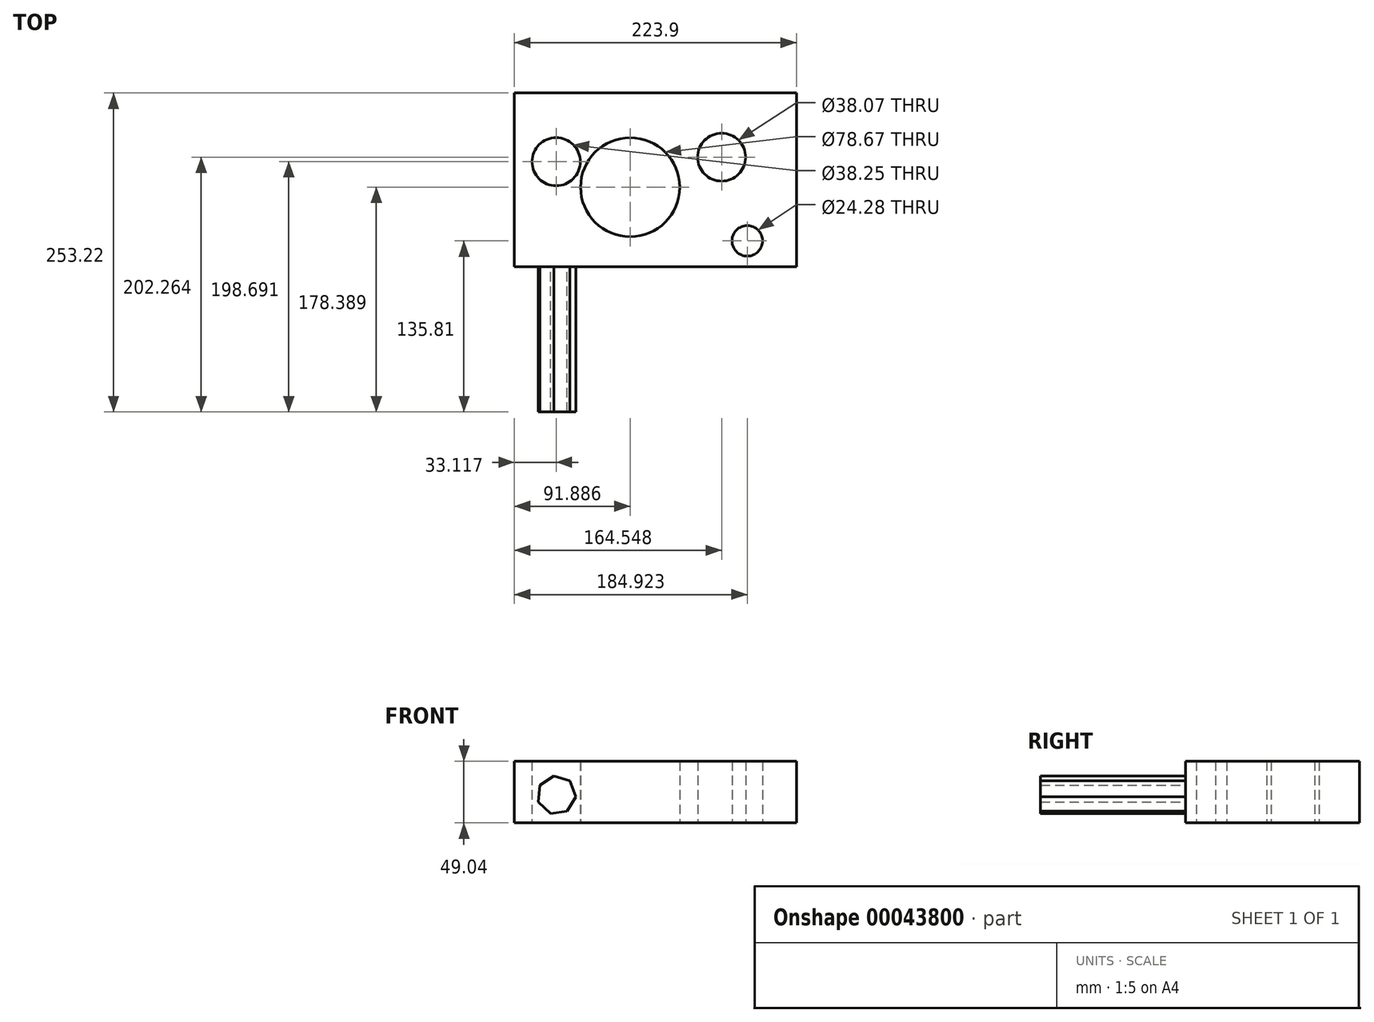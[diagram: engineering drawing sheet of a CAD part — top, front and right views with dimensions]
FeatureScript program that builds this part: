
annotation { "Feature Type Name" : "Feature", "Feature Type Description" : "" }
export const myFeature = defineFeature(function(context is Context, id is Id, definition is map)
    precondition{}
    {
        {
            var Q0;
            Q0=qCreatedBy(makeId("Top.planeOp"),FACE);
            var sketch = newSketch(context, id + "F0", { "sketchPlane" : qUnion([Q0])});
            skLineSegment(sketch, "E0.bottom", {"start": v(-84.37, -20.67) * mm, "end": v(139.53, -20.67) * mm});
            skLineSegment(sketch, "E0.top", {"start": v(-84.37, 117.4) * mm, "end": v(139.53, 117.4) * mm});
            skLineSegment(sketch, "E0.left", {"start": v(-84.37, -20.67) * mm, "end": v(-84.37, 117.4) * mm});
            skLineSegment(sketch, "E0.right", {"start": v(139.53, -20.67) * mm, "end": v(139.53, 117.4) * mm});
            skCircle(sketch, "E1", {"center": v(-51.25, 62.88) * mm, "radius": 19.13 * mm});
            skCircle(sketch, "E2", {"center": v(7.52, 42.58) * mm, "radius": 39.34 * mm});
            skCircle(sketch, "E3", {"center": v(80.18, 66.45) * mm, "radius": 19.03 * mm});
            skCircle(sketch, "E4", {"center": v(100.55, 0) * mm, "radius": 12.14 * mm});
            skSolve(sketch);
        }
        {
            var Q0;
            Q0 = qSketchRegion(id + "F0", true);
            extrude(context, id + "F1", {"entities" : qUnion([Q0]), "depth" : 49.04 * mm});
        }
        {
            var Q0;
            Q0=makeQuery(id+"F1.opExtrude","SWEPT_FACE",FACE,{"disambiguationData":[OSD([sQuery(id+"F0.wireOp",EDGE,"E0.bottom")])]});
            var sketch = newSketch(context, id + "F2", { "sketchPlane" : qUnion([Q0])});
            skCircle(sketch, "E5.cCircle", {"center": v(-51, 22.15) * mm, "radius": 13.87 * mm, "construction": true});
            skLineSegment(sketch, "E5.0", {"start": v(-40.38, 33.3) * mm, "end": v(-35.65, 20.8) * mm});
            skLineSegment(sketch, "E5.1", {"start": v(-35.65, 20.8) * mm, "end": v(-42.48, 9.32) * mm});
            skLineSegment(sketch, "E5.2", {"start": v(-42.48, 9.32) * mm, "end": v(-55.72, 7.5) * mm});
            skLineSegment(sketch, "E5.3", {"start": v(-55.72, 7.5) * mm, "end": v(-65.4, 16.7) * mm});
            skLineSegment(sketch, "E5.4", {"start": v(-65.4, 16.7) * mm, "end": v(-64.23, 30.02) * mm});
            skLineSegment(sketch, "E5.5", {"start": v(-64.23, 30.02) * mm, "end": v(-53.1, 37.4) * mm});
            skLineSegment(sketch, "E5.6", {"start": v(-53.1, 37.4) * mm, "end": v(-40.38, 33.3) * mm});
            skPoint(sketch, "E5.0.midPoint", {"position": v(-38.01, 27.05) * mm});
            skSolve(sketch);
        }
        {
            var Q0;
            Q0 = qSketchRegion(id + "F2", true);
            extrude(context, id + "F3", {"entities" : qUnion([Q0]), "operationType" : NewBodyOperationType.ADD, "depth" : 115.14 * mm});
        }
    });
